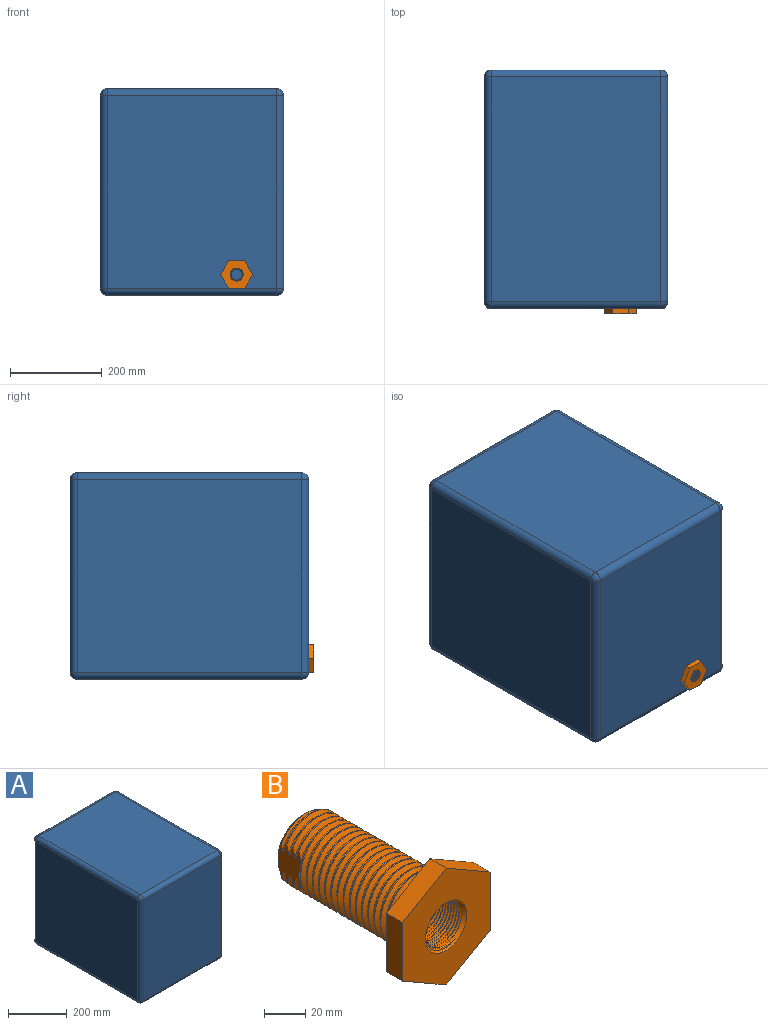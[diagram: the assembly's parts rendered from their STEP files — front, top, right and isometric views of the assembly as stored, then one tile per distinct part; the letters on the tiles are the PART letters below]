
ASSEMBLY  parts=2 mates=1
PART A: 26 faces, bbox 400x520x450 mm
  f0: plane 420x370mm, normal (0,1,0), area 155400mm2, adj f14,f19,f22,f25
  f1: plane 490x420mm, normal (-1,0,0), area 205800mm2, adj f11,f20,f21,f25
  f2: plane 420x370mm, normal (0,-1,0), area 155400mm2, adj f6,f10,f11,f12
  f3: plane 490x420mm, normal (1,0,0), area 205800mm2, adj f6,f9,f13,f14
  f4: plane 490x370mm, normal (0,0,1), area 181300mm2, adj f9,f10,f19,f20
  f5: plane 490x370mm, normal (0,0,-1), area 181300mm2, adj f12,f13,f21,f22
  f6: cylinder r=15mm len=420mm, axis (0,0,1), area 9896mm2, adj f2,f3,f7,f8
  f7: sphere r=15mm, area 353.4mm2, adj f6,f9,f10
  f8: sphere r=15mm, area 353.4mm2, adj f6,f12,f13
  f9: cylinder r=15mm len=490mm, axis (0,-1,0), area 11545.4mm2, adj f3,f4,f7,f15
  f10: cylinder r=15mm len=370mm, axis (-1,0,0), area 8717.9mm2, adj f2,f4,f7,f16
  f11: cylinder r=15mm len=420mm, axis (0,0,-1), area 9896mm2, adj f1,f2,f16,f17
  f12: cylinder r=15mm len=370mm, axis (1,0,0), area 8717.9mm2, adj f2,f5,f8,f17
  f13: cylinder r=15mm len=490mm, axis (0,1,0), area 11545.4mm2, adj f3,f5,f8,f18
  f14: cylinder r=15mm len=420mm, axis (0,0,-1), area 9896mm2, adj f0,f3,f15,f18
  f15: sphere r=15mm, area 353.4mm2, adj f9,f14,f19
  f16: sphere r=15mm, area 353.4mm2, adj f10,f11,f20
  f17: sphere r=15mm, area 353.4mm2, adj f11,f12,f21
  f18: sphere r=15mm, area 353.4mm2, adj f13,f14,f22
  f19: cylinder r=15mm len=370mm, axis (1,0,0), area 8717.9mm2, adj f0,f4,f15,f23
  f20: cylinder r=15mm len=490mm, axis (0,1,0), area 11545.4mm2, adj f1,f4,f16,f23
  f21: cylinder r=15mm len=490mm, axis (0,-1,0), area 11545.4mm2, adj f1,f5,f17,f24
  f22: cylinder r=15mm len=370mm, axis (-1,0,0), area 8717.9mm2, adj f0,f5,f18,f24
  f23: sphere r=15mm, area 353.4mm2, adj f19,f20,f25
  f24: sphere r=15mm, area 353.4mm2, adj f21,f22,f25
  f25: cylinder r=15mm len=420mm, axis (0,0,1), area 9896mm2, adj f0,f1,f23,f24
PART B: 60 faces, bbox 61.6x99.7x70.9 mm
  f0: plane 34.93x34.61mm, normal (0,1,0), area 319.8mm2, adj f13,f14,f15,f17,f53
  f1: plane 69.66x60.33mm, normal (0,-1,0), area 2514.3mm2, adj f40,f41,f42,f43,f44,f45,f47
  f2: bspline ~73.99x41.27mm, area 5392mm2, adj f4,f6,f17,f18,f46
  f3: bspline ~74.49x41.73mm, area 5562.8mm2, adj f4,f6,f15,f16,f17,f19,f46
  f4: cylinder r=18.35mm len=70.71mm, axis (0,-1,0), area 1271.6mm2, adj f2,f3,f15,f21,f46
  f5: plane 69.66x60.33mm, normal (0,1,0), area 1813.5mm2, adj f6,f40,f41,f42,f43,f44,f45,f46
  f6: cylinder r=20.64mm len=72.57mm, axis (0,-1,0), area 1123.9mm2, adj f2,f3,f5,f17
  f7: cylinder r=20.64mm len=34.61mm, axis (0,-1,0), area 21.7mm2, adj f15,f17,f21,f34
  f8: cylinder r=20.64mm len=34.61mm, axis (0,-1,0), area 21.7mm2, adj f15,f17,f20,f25
  f9: cylinder r=20.64mm len=34.61mm, axis (0,-1,0), area 21.7mm2, adj f15,f17,f31,f36
  f10: cylinder r=20.64mm len=34.61mm, axis (0,-1,0), area 21.7mm2, adj f15,f17,f22,f27
  f11: cylinder r=20.64mm len=34.61mm, axis (0,-1,0), area 21.7mm2, adj f15,f17,f28,f33
  f12: cylinder r=20.64mm len=17.3mm, axis (0,-1,0), area 6.6mm2, adj f14,f15,f24,f39
  f13: cone r=20.64mm half-angle=45deg, axis (0,-1,0), area 120.8mm2, adj f0,f15,f17,f30
  f14: cone r=20.64mm half-angle=45deg, axis (0,-1,0), area 131.4mm2, adj f0,f12,f15,f17,f24,f37,f38,f39
  f15: plane 22.99x16.38mm, normal (1,0,0), area 254.9mm2, adj f0,f3,f4,f7,f8,f9,f10,f11
  f16: plane 19.36x2.76mm, normal (0,1,0), area 31.6mm2, adj f3,f15
  f17: plane 23.75x17.14mm, normal (-1,0,0), area 261.3mm2, adj f0,f2,f3,f6,f7,f8,f9,f10
  f18: plane 15.11x1.75mm, normal (0,1,0), area 15.4mm2, adj f2,f17
  f19: cylinder r=18.35mm len=34.61mm, axis (0,-1,0), area 47.7mm2, adj f3,f15,f17,f20
  f20: bspline ~41.62x19.52mm, area 114.6mm2, adj f8,f15,f17,f19
  f21: bspline ~41.6x19.5mm, area 114.5mm2, adj f4,f7,f15,f17
  f22: bspline ~41.62x19.52mm, area 114.6mm2, adj f10,f15,f17,f23
  f23: cylinder r=18.35mm len=34.61mm, axis (0,-1,0), area 47.7mm2, adj f15,f17,f22,f24
  f24: bspline ~41.62x19.52mm, area 109.1mm2, adj f12,f14,f15,f17,f23
  f25: bspline ~41.62x19.52mm, area 114.6mm2, adj f8,f15,f17,f26
  f26: cylinder r=18.35mm len=34.61mm, axis (0,-1,0), area 47.7mm2, adj f15,f17,f25,f27
  f27: bspline ~41.62x19.52mm, area 114.6mm2, adj f10,f15,f17,f26
  f28: bspline ~41.62x19.52mm, area 114.6mm2, adj f11,f15,f17,f29
  f29: cylinder r=18.35mm len=34.61mm, axis (0,-1,0), area 47.7mm2, adj f15,f17,f28,f30
  f30: bspline ~39.7x18.55mm, area 48mm2, adj f13,f15,f17,f29
  f31: bspline ~41.62x19.52mm, area 114.6mm2, adj f9,f15,f17,f32
  f32: cylinder r=18.35mm len=34.61mm, axis (0,-1,0), area 47.7mm2, adj f15,f17,f31,f33
  f33: bspline ~41.62x19.52mm, area 114.6mm2, adj f11,f15,f17,f32
  f34: bspline ~41.62x19.52mm, area 114.6mm2, adj f7,f15,f17,f35
  f35: cylinder r=18.35mm len=34.61mm, axis (0,-1,0), area 47.7mm2, adj f15,f17,f34,f36
  f36: bspline ~38.93x14.53mm, area 114.6mm2, adj f9,f15,f17,f35
  f37: cylinder r=18.35mm len=28.45mm, axis (0,-1,0), area 21.3mm2, adj f14,f15,f38,f39
  f38: bspline ~6.22x3.45mm, area 0.4mm2, adj f14,f15,f37
  f39: bspline ~32.01x14.54mm, area 53.2mm2, adj f12,f14,f15,f37
  f40: plane 30.16x17.41mm, normal (0.5,0,0.87), area 389.2mm2, adj f1,f5,f41,f45
  f41: plane 34.83x11.18mm, normal (1,0,0), area 389.2mm2, adj f1,f5,f40,f42
  f42: plane 30.16x17.41mm, normal (0.5,0,-0.87), area 389.2mm2, adj f1,f5,f41,f43
  f43: plane 30.16x17.41mm, normal (-0.5,0,-0.87), area 389.2mm2, adj f1,f5,f42,f44
  f44: plane 34.83x11.18mm, normal (-1,0,0), area 389.2mm2, adj f1,f5,f43,f45
  f45: plane 30.16x17.41mm, normal (-0.5,0,0.87), area 389.2mm2, adj f1,f5,f40,f44
  f46: cone r=20.64mm half-angle=45deg, axis (0,-1,0), area 225.7mm2, adj f2,f3,f4,f5
  f47: cone r=14.24mm half-angle=45deg, axis (0,-1,0), area 182.5mm2, adj f1,f49,f50,f51,f52
  f48: plane 24.94x24.74mm, normal (0,-1,0), area 118.9mm2, adj f49,f50,f51,f52,f59
  f49: bspline ~26.93x26.91mm, area 964.9mm2, adj f47,f48,f50,f52
  f50: bspline ~24.63x24.61mm, area 342.2mm2, adj f47,f48,f49,f51
  f51: bspline ~26.91x26.9mm, area 918.6mm2, adj f47,f48,f50,f52
  f52: cone r=13.33mm half-angle=1.8deg, axis (0,-1,0), area 172.6mm2, adj f47,f48,f49,f51
  f53: cone r=14.24mm half-angle=45deg, axis (0,1,0), area 182.5mm2, adj f0,f55,f56,f57,f58
  f54: plane 24.94x24.74mm, normal (0,1,0), area 118.9mm2, adj f55,f56,f57,f58,f59
  f55: bspline ~24.63x24.61mm, area 342.2mm2, adj f53,f54,f56,f57
  f56: bspline ~26.91x26.9mm, area 918.6mm2, adj f53,f54,f55,f58
  f57: bspline ~26.93x26.91mm, area 964.9mm2, adj f53,f54,f55,f58
  f58: cone r=13.33mm half-angle=1.8deg, axis (0,1,0), area 172.6mm2, adj f53,f54,f56,f57
  f59: cylinder r=10.46mm len=58.12mm, axis (0,-1,0), area 3821.2mm2, adj f48,f54
PLACE A t=(-35.94,112.31,34.59)mm
PLACE B rot(axis=(0,-1,0),90deg) t=(61.45,-109.65,79.59)mm
MATE fastened B.f6 <-> A.f2  axis (0,1,0) through (61.45,-147.69,79.59)mm
